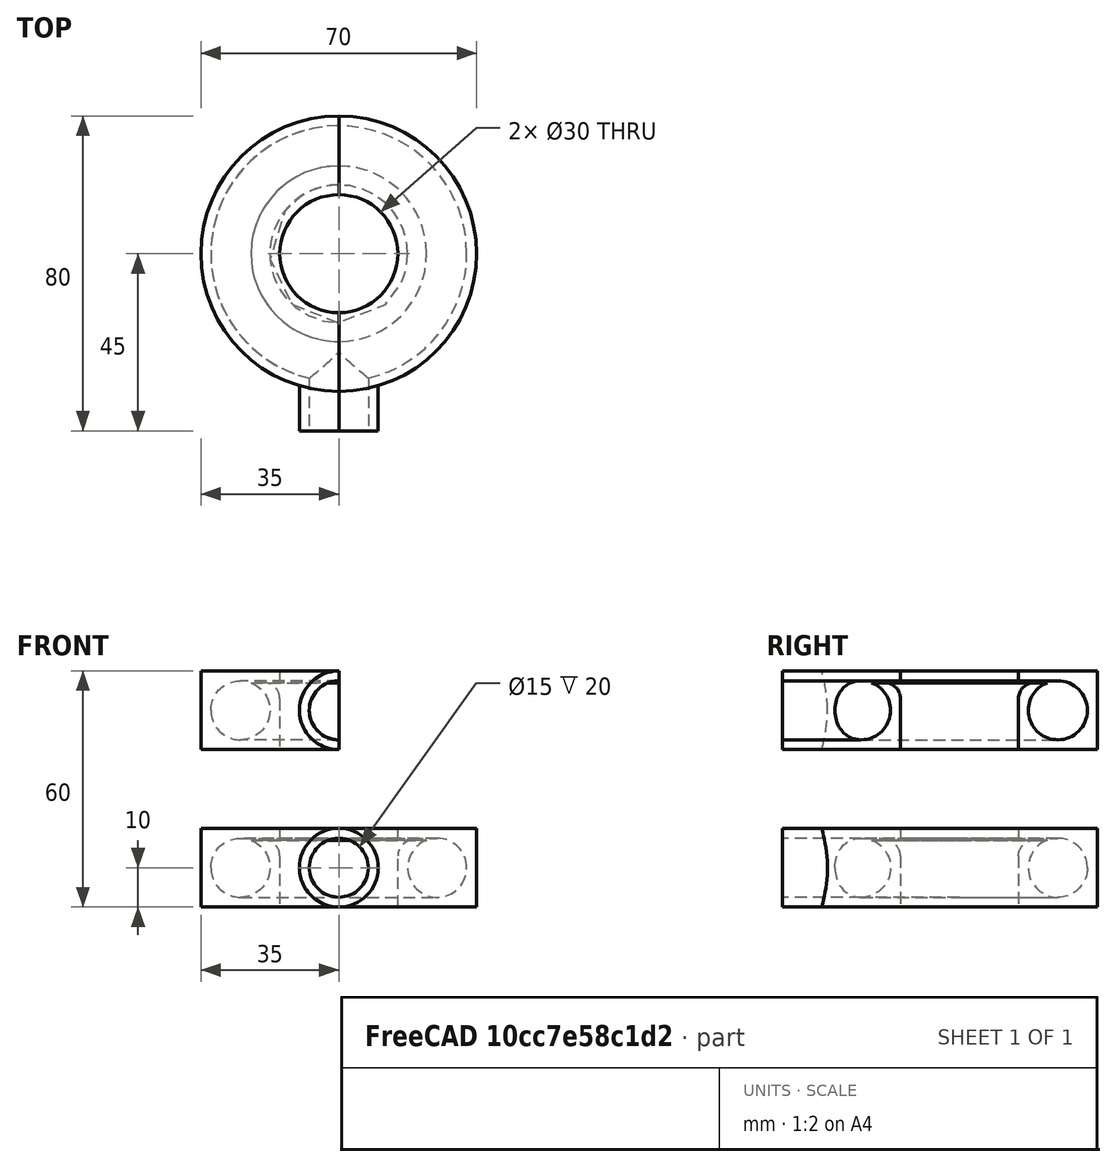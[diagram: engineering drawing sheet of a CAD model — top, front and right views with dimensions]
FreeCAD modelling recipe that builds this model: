
FCSTD DOCUMENT  (FreeCAD 1.0R)
Label: circle knife air
License: All rights reserved
objects: TechDraw::DrawViewDimension×13, Sketcher::SketchObject×11, PartDesign::Plane×6, PartDesign::Pocket×5, PartDesign::Pad×4, TechDraw::DrawProjGroupItem×4, PartDesign::Groove×2, PartDesign::Fillet×2, PartDesign::Body×2, TechDraw::DrawProjGroup×2, TechDraw::DrawSVGTemplate×1, TechDraw::DrawPage×1
note: 87 computed .brp shape members not serialized (recipe doc carries the construction recipe); baked Part::Feature solids carry a one-line shape summary decoded from their .brp

FEATURE [Sketcher::SketchObject] Sketch
  ArcFitTolerance = 1e-06
  AttachmentSupport = -> [XY_Plane]
  FullyConstrained = true
  MakeInternals = false
  MapMode = 5
  sketch-geometry (2):
    g0: Circle CenterX=0 CenterY=0 CenterZ=0 NormalX=0 NormalY=0 NormalZ=1 AngleXU=0 Radius=15
    g1: Circle CenterX=0 CenterY=0 CenterZ=0 NormalX=0 NormalY=0 NormalZ=1 AngleXU=0 Radius=35
  constraints (4):
    c: Diameter(g0) = 30
    c: Coincident(g0,g-1)
    c: Diameter(g1) = 70
    c: Coincident(g1,g0)
FEATURE [PartDesign::Pad] Pad
  Direction = (0,0,1)
  Length = 20
  Length2 = 10
  Profile = -> Sketch
  ReferenceAxis = -> Sketch [N_Axis]
  Refine = true
  Suppressed = false
  Type = 0
FEATURE [PartDesign::Plane] DatumPlane
  AttachmentOffset = pos=(0,0,0) rot=(1,0,0;1.5708rad)
  AttachmentSupport = -> [Pad]
  Length = 60
  MapMode = 5
  Placement = pos=(0,0,20) rot=(1,0,0;1.5708rad)
  ResizeMode = 0
  Width = 60
FEATURE [Sketcher::SketchObject] Sketch001
  ArcFitTolerance = 1e-06
  AttachmentSupport = -> [DatumPlane]
  ExternalGeometry = -> [Pad]
  FullyConstrained = true
  MakeInternals = false
  MapMode = 5
  Placement = pos=(0,0,20) rot=(1,0,0;1.5708rad)
  sketch-geometry (1):
    g0: Circle CenterX=25 CenterY=-10 CenterZ=0 NormalX=0 NormalY=0 NormalZ=1 AngleXU=0 Radius=7.5
  constraints (3):
    c: Diameter(g0) = 15
    c: Distance(g0,g-3) = 10
    c: DistanceY(g-3,g0) = 10
FEATURE [PartDesign::Groove] Groove
  Angle = 360
  Angle2 = 60
  Axis = (0,2e-16,1)
  Base = (0,0,20)
  BaseFeature = -> Pad
  Profile = -> Sketch001
  ReferenceAxis = -> Sketch001 [V_Axis]
  Refine = true
  Suppressed = false
  Type = 0
FEATURE [PartDesign::Plane] DatumPlane001
  AttachmentOffset = pos=(0,0,-2.5) rot=(0,0,1;0rad)
  AttachmentSupport = -> [Groove]
  Length = 60
  MapMode = 5
  Placement = pos=(0,0,17.5) rot=(0,0,1;0rad)
  ResizeMode = 0
  Width = 60
FEATURE [Sketcher::SketchObject] Sketch002
  ArcFitTolerance = 1e-06
  AttachmentSupport = -> [DatumPlane001]
  FullyConstrained = true
  MakeInternals = false
  MapMode = 5
  Placement = pos=(0,0,17.5) rot=(0,0,1;0rad)
  sketch-geometry (1):
    g0: Circle CenterX=0 CenterY=0 CenterZ=0 NormalX=0 NormalY=0 NormalZ=1 AngleXU=0 Radius=25
  constraints (2):
    c: Diameter(g0) = 50
    c: Coincident(g0,g-1)
FEATURE [PartDesign::Pocket] Pocket
  BaseFeature = -> Groove
  Direction = (0,0,-1)
  Length = 0.5
  Length2 = 5
  Profile = -> Sketch002
  ReferenceAxis = -> Sketch002 [N_Axis]
  Refine = true
  Suppressed = false
  Type = 0
FEATURE [PartDesign::Plane] DatumPlane002
  AttachmentOffset = pos=(0,-35,0) rot=(0,0.707107,0.707107;3.14159rad)
  AttachmentSupport = -> [Pocket]
  Length = 60
  MapMode = 5
  Placement = pos=(0,-35,20) rot=(0,0.707107,0.707107;3.14159rad)
  ResizeMode = 0
  Width = 60
FEATURE [Sketcher::SketchObject] Sketch003
  ArcFitTolerance = 1e-06
  AttachmentSupport = -> [DatumPlane002]
  ExternalGeometry = -> [Pocket]
  FullyConstrained = true
  MakeInternals = false
  MapMode = 5
  Placement = pos=(0,-35,20) rot=(0,0.707107,0.707107;3.14159rad)
  sketch-geometry (1):
    g0: Circle CenterX=0 CenterY=-10 CenterZ=0 NormalX=0 NormalY=0 NormalZ=1 AngleXU=0 Radius=7.5
  constraints (3):
    c: Diameter(g0) = 15
    c: PointOnObject(g0,g-2)
    c: Distance(g0,g-3) = 10
FEATURE [PartDesign::Pocket] Pocket001
  BaseFeature = -> Pocket
  Direction = (0,-1,2e-16)
  Length = 10
  Length2 = 5
  Profile = -> Sketch003 [Edge1]
  ReferenceAxis = -> Sketch003 [N_Axis]
  Refine = true
  Reversed = true
  Suppressed = false
  Type = 0
FEATURE [Sketcher::SketchObject] Sketch004
  ArcFitTolerance = 1e-06
  AttachmentSupport = -> [DatumPlane002]
  FullyConstrained = true
  MakeInternals = false
  MapMode = 5
  Placement = pos=(0,-35,20) rot=(0,0.707107,0.707107;3.14159rad)
  sketch-geometry (2):
    g0: Circle CenterX=0 CenterY=-10 CenterZ=0 NormalX=0 NormalY=0 NormalZ=1 AngleXU=0 Radius=7.5
    g1: Circle CenterX=0 CenterY=-10 CenterZ=0 NormalX=0 NormalY=0 NormalZ=1 AngleXU=0 Radius=10
  constraints (5):
    c: Diameter(g0) = 15
    c: PointOnObject(g0,g-2)
    c: DistanceY(g0,g-1) = 10
    c: Diameter(g1) = 20
    c: Coincident(g1,g0)
FEATURE [PartDesign::Pad] Pad001
  BaseFeature = -> Pocket001
  Direction = (0,1,-2e-16)
  Length = 2
  Length2 = 10
  Profile = -> Sketch004
  ReferenceAxis = -> Sketch004 [N_Axis]
  Refine = true
  Suppressed = false
  Type = 4
FEATURE [PartDesign::Fillet] Fillet
  Base = -> Pad001 [Edge15]
  BaseFeature = -> Pad001
  Radius = 4
  Refine = true
  SupportTransform = false
  Suppressed = false
  UseAllEdges = false
FEATURE [PartDesign::Body] Body
  AllowCompound = false
  Group = -> [Sketch,Pad,DatumPlane,Sketch001,Groove,DatumPlane001,Sketch002,Pocket,DatumPlane002,Sketch003,Pocket001,Sketch004,Pad001,Fillet]
  Origin = -> Origin
  Tip = -> Fillet
FEATURE [Sketcher::SketchObject] Sketch005
  ArcFitTolerance = 1e-06
  AttachmentSupport = -> [XY_Plane001]
  FullyConstrained = true
  MakeInternals = false
  MapMode = 5
  sketch-geometry (2):
    g0: Circle CenterX=0 CenterY=0 CenterZ=0 NormalX=0 NormalY=0 NormalZ=1 AngleXU=0 Radius=15
    g1: Circle CenterX=0 CenterY=0 CenterZ=0 NormalX=0 NormalY=0 NormalZ=1 AngleXU=0 Radius=35
  constraints (4):
    c: Diameter(g0) = 30
    c: Coincident(g0,g-1)
    c: Diameter(g1) = 70
    c: Coincident(g1,g0)
FEATURE [PartDesign::Pad] Pad002
  Direction = (0,0,1)
  Length = 20
  Length2 = 10
  Profile = -> Sketch005
  ReferenceAxis = -> Sketch005 [N_Axis]
  Refine = true
  Suppressed = false
  Type = 0
FEATURE [PartDesign::Plane] DatumPlane003
  AttachmentOffset = pos=(0,0,0) rot=(1,0,0;1.5708rad)
  AttachmentSupport = -> [Pad002]
  Length = 60
  MapMode = 5
  Placement = pos=(0,0,20) rot=(1,0,0;1.5708rad)
  ResizeMode = 0
  Width = 60
FEATURE [Sketcher::SketchObject] Sketch006
  ArcFitTolerance = 1e-06
  AttachmentSupport = -> [DatumPlane003]
  ExternalGeometry = -> [Pad002]
  FullyConstrained = true
  MakeInternals = false
  MapMode = 5
  Placement = pos=(0,0,20) rot=(1,0,0;1.5708rad)
  sketch-geometry (1):
    g0: Circle CenterX=25 CenterY=-10 CenterZ=0 NormalX=0 NormalY=0 NormalZ=1 AngleXU=0 Radius=7.5
  constraints (3):
    c: Diameter(g0) = 15
    c: Distance(g0,g-3) = 10
    c: DistanceY(g-3,g0) = 10
FEATURE [PartDesign::Groove] Groove001
  Angle = 360
  Angle2 = 60
  Axis = (0,2e-16,1)
  Base = (0,0,20)
  BaseFeature = -> Pad002
  Profile = -> Sketch006
  ReferenceAxis = -> Sketch006 [V_Axis]
  Refine = true
  Suppressed = false
  Type = 0
FEATURE [PartDesign::Plane] DatumPlane004
  AttachmentOffset = pos=(0,0,-2.5) rot=(0,0,1;0rad)
  AttachmentSupport = -> [Groove001]
  Length = 60
  MapMode = 5
  Placement = pos=(0,0,17.5) rot=(0,0,1;0rad)
  ResizeMode = 0
  Width = 60
FEATURE [Sketcher::SketchObject] Sketch007
  ArcFitTolerance = 1e-06
  AttachmentSupport = -> [DatumPlane004]
  FullyConstrained = true
  MakeInternals = false
  MapMode = 5
  Placement = pos=(0,0,17.5) rot=(0,0,1;0rad)
  sketch-geometry (1):
    g0: Circle CenterX=0 CenterY=0 CenterZ=0 NormalX=0 NormalY=0 NormalZ=1 AngleXU=0 Radius=25
  constraints (2):
    c: Diameter(g0) = 50
    c: Coincident(g0,g-1)
FEATURE [PartDesign::Pocket] Pocket002
  BaseFeature = -> Groove001
  Direction = (0,0,-1)
  Length = 0.5
  Length2 = 5
  Profile = -> Sketch007
  ReferenceAxis = -> Sketch007 [N_Axis]
  Refine = true
  Suppressed = false
  Type = 0
FEATURE [PartDesign::Plane] DatumPlane005
  AttachmentOffset = pos=(0,-35,0) rot=(0,0.707107,0.707107;3.14159rad)
  AttachmentSupport = -> [Pocket002]
  Length = 60
  MapMode = 5
  Placement = pos=(0,-35,20) rot=(0,0.707107,0.707107;3.14159rad)
  ResizeMode = 0
  Width = 60
FEATURE [Sketcher::SketchObject] Sketch008
  ArcFitTolerance = 1e-06
  AttachmentSupport = -> [DatumPlane005]
  ExternalGeometry = -> [Pocket002]
  FullyConstrained = true
  MakeInternals = false
  MapMode = 5
  Placement = pos=(0,-35,20) rot=(0,0.707107,0.707107;3.14159rad)
  sketch-geometry (1):
    g0: Circle CenterX=0 CenterY=-10 CenterZ=0 NormalX=0 NormalY=0 NormalZ=1 AngleXU=0 Radius=7.5
  constraints (3):
    c: Diameter(g0) = 15
    c: PointOnObject(g0,g-2)
    c: Distance(g0,g-3) = 10
FEATURE [PartDesign::Pocket] Pocket003
  BaseFeature = -> Pocket002
  Direction = (0,-1,2e-16)
  Length = 10
  Length2 = 5
  Profile = -> Sketch008 [Edge1]
  ReferenceAxis = -> Sketch008 [N_Axis]
  Refine = true
  Reversed = true
  Suppressed = false
  Type = 0
FEATURE [Sketcher::SketchObject] Sketch009
  ArcFitTolerance = 1e-06
  AttachmentSupport = -> [DatumPlane005]
  FullyConstrained = true
  MakeInternals = false
  MapMode = 5
  Placement = pos=(0,-35,20) rot=(0,0.707107,0.707107;3.14159rad)
  sketch-geometry (2):
    g0: Circle CenterX=0 CenterY=-10 CenterZ=0 NormalX=0 NormalY=0 NormalZ=1 AngleXU=0 Radius=7.5
    g1: Circle CenterX=0 CenterY=-10 CenterZ=0 NormalX=0 NormalY=0 NormalZ=1 AngleXU=0 Radius=10
  constraints (5):
    c: Diameter(g0) = 15
    c: PointOnObject(g0,g-2)
    c: DistanceY(g0,g-1) = 10
    c: Diameter(g1) = 20
    c: Coincident(g1,g0)
FEATURE [PartDesign::Pad] Pad003
  BaseFeature = -> Pocket003
  Direction = (0,1,-2e-16)
  Length = 2
  Length2 = 10
  Profile = -> Sketch009
  ReferenceAxis = -> Sketch009 [N_Axis]
  Refine = true
  Suppressed = false
  Type = 4
FEATURE [PartDesign::Fillet] Fillet001
  Base = -> Pad003 [Edge15]
  BaseFeature = -> Pad003
  Radius = 4
  Refine = true
  SupportTransform = false
  Suppressed = false
  UseAllEdges = false
FEATURE [Sketcher::SketchObject] Sketch010
  ArcFitTolerance = 1e-06
  AttachmentSupport = -> [Fillet001]
  FullyConstrained = false
  MakeInternals = false
  MapMode = 5
  Placement = pos=(0,0,20) rot=(0,0,1;0rad)
  sketch-geometry (4):
    g0: LineSegment StartX=0 StartY=40.2056 StartZ=0 EndX=0 EndY=-51.8997 EndZ=0
    g1: LineSegment StartX=0 StartY=-51.8997 StartZ=0 EndX=42.0981 EndY=-51.8997 EndZ=0
    g2: LineSegment StartX=42.0981 StartY=-51.8997 StartZ=0 EndX=42.0981 EndY=40.2056 EndZ=0
    g3: LineSegment StartX=42.0981 StartY=40.2056 StartZ=0 EndX=0 EndY=40.2056 EndZ=0
  constraints (9):
    c: Coincident(g0,g1)
    c: Coincident(g1,g2)
    c: Coincident(g2,g3)
    c: Coincident(g3,g0)
    c: Vertical(g0)
    c: Vertical(g2)
    c: Horizontal(g1)
    c: Horizontal(g3)
    c: PointOnObject(g0,g-2)
FEATURE [PartDesign::Pocket] Pocket004
  BaseFeature = -> Fillet001
  Direction = (0,0,-1)
  Length = 5
  Length2 = 5
  Profile = -> Sketch010
  ReferenceAxis = -> Sketch010 [N_Axis]
  Refine = true
  Suppressed = false
  Type = 1
FEATURE [PartDesign::Body] Body001
  AllowCompound = false
  Group = -> [Sketch005,Pad002,DatumPlane003,Sketch006,Groove001,DatumPlane004,Sketch007,Pocket002,DatumPlane005,Sketch008,Pocket003,Sketch009,Pad003,Fillet001,Sketch010,Pocket004]
  Origin = -> Origin001
  Placement = pos=(0,0,40) rot=(0,0,1;0rad)
  Tip = -> Pocket004
FEATURE [TechDraw::DrawSVGTemplate] Template
  EditableTexts = approval_person=B. Hecate; creator=A. Nemesis; date_of_issue=27/10/25; document_type=Assembly Drawing; general_tolerances=ISO 2768-m; identification_number=DN; language_code=EN; part_material=Stainless steel Mat.No. 1.4301; revision_index=AAA; sheet_number=1 / 1; sheet_scale=1 : 1; title=circle knife air
  Height = 210
  Orientation = 1
  Template = <path>
  Width = 297
FEATURE [TechDraw::DrawProjGroupItem] View  label="Front001"
  CoarseView = false
  Direction = (1,-1e-16,0)
  Focus = 100
  HardHidden = false
  IsoCount = 0
  IsoHidden = false
  IsoVisible = false
  LockPosition = true
  Perspective = false
  Rotation = 0
  RotationVector = (1,0,0)
  ScaleType = 2
  ScrubCount = 1
  SeamHidden = false
  SeamVisible = false
  SmoothHidden = false
  SmoothVisible = true
  Source = -> [Body001]
  Type = 0
  X = 0
  XDirection = (1e-16,1,0)
  Y = 0
FEATURE [TechDraw::DrawProjGroupItem] View001  label="Front"
  CoarseView = false
  Direction = (0,-1,0)
  Focus = 100
  HardHidden = false
  IsoCount = 0
  IsoHidden = false
  IsoVisible = false
  LockPosition = true
  Perspective = false
  Rotation = 0
  RotationVector = (1,0,0)
  ScaleType = 2
  ScrubCount = 1
  SeamHidden = false
  SeamVisible = false
  SmoothHidden = false
  SmoothVisible = true
  Source = -> [Body]
  Type = 0
  X = 0
  XDirection = (1,0,0)
  Y = 0
FEATURE [TechDraw::DrawProjGroupItem] ProjItem  label="Top"
  CoarseView = false
  Direction = (0,0,1)
  Focus = 100
  HardHidden = false
  IsoCount = 0
  IsoHidden = false
  IsoVisible = false
  LockPosition = false
  Perspective = false
  Rotation = 0
  RotationVector = (1,0,0)
  ScaleType = 0
  ScrubCount = 1
  SeamHidden = false
  SeamVisible = false
  SmoothHidden = false
  SmoothVisible = true
  Source = -> [Body]
  Type = 4
  X = 0
  XDirection = (1,0,0)
  Y = -65
FEATURE [TechDraw::DrawProjGroup] ProjGroup
  Anchor = -> View001
  AutoDistribute = true
  LockPosition = false
  ProjectionType = 0
  Rotation = 0
  ScaleType = 0
  Source = -> [Body]
  Views = -> [View001,ProjItem]
  X = 194.823
  Y = 180.18
  spacingX = 15
  spacingY = 15
FEATURE [TechDraw::DrawViewDimension] Dimension
  AngleOverride = false
  Arbitrary = false
  ArbitraryTolerances = false
  BoxCorners = (2) [(-35,-40,-1e-07),(35,40,1e-07)]
  EqualTolerance = true
  ExtensionAngle = 0
  FormatSpec = ⌀%.2w
  FormatSpecOverTolerance = %+.2w
  FormatSpecUnderTolerance = %+.2w
  Inverted = false
  LineAngle = 0
  LockPosition = false
  MeasureType = 1
  OverTolerance = 0
  References2D = -> [ProjItem]
  Rotation = 0
  ScaleType = 0
  TheoreticalExact = false
  Type = 5
  UnderTolerance = 0
  X = 47.9854
  Y = 2.55014
FEATURE [TechDraw::DrawViewDimension] Dimension001
  AngleOverride = false
  Arbitrary = false
  ArbitraryTolerances = false
  BoxCorners = (2) [(-35,-40,-1e-07),(35,40,1e-07)]
  EqualTolerance = true
  ExtensionAngle = 0
  FormatSpec = R%.2w
  FormatSpecOverTolerance = %+.2w
  FormatSpecUnderTolerance = %+.2w
  Inverted = false
  LineAngle = 0
  LockPosition = false
  MeasureType = 1
  OverTolerance = 0
  References2D = -> [ProjItem]
  Rotation = 0
  ScaleType = 0
  TheoreticalExact = false
  Type = 4
  UnderTolerance = 0
  X = 50.0135
  Y = 13.0677
FEATURE [TechDraw::DrawViewDimension] Dimension002
  AngleOverride = false
  Arbitrary = false
  ArbitraryTolerances = false
  BoxCorners = (2) [(-35,-40,-1e-07),(35,40,1e-07)]
  EqualTolerance = true
  ExtensionAngle = 0
  FormatSpec = %.2w
  FormatSpecOverTolerance = %+.2w
  FormatSpecUnderTolerance = %+.2w
  Inverted = false
  LineAngle = 0
  LockPosition = false
  MeasureType = 1
  OverTolerance = 0
  References2D = -> [ProjItem]
  Rotation = 0
  ScaleType = 0
  TheoreticalExact = false
  Type = 2
  UnderTolerance = 0
  X = 22.9103
  Y = -34.2705
FEATURE [TechDraw::DrawViewDimension] Dimension003
  AngleOverride = false
  Arbitrary = false
  ArbitraryTolerances = false
  BoxCorners = (2) [(-35,-40,-1e-07),(35,40,1e-07)]
  EqualTolerance = true
  ExtensionAngle = 0
  FormatSpec = %.2w
  FormatSpecOverTolerance = %+.2w
  FormatSpecUnderTolerance = %+.2w
  Inverted = false
  LineAngle = 0
  LockPosition = false
  MeasureType = 1
  OverTolerance = 0
  References2D = -> [ProjItem]
  Rotation = 0
  ScaleType = 0
  TheoreticalExact = false
  Type = 0
  UnderTolerance = 0
  X = -22.6694
  Y = -43.2394
FEATURE [TechDraw::DrawViewDimension] Dimension004
  AngleOverride = false
  Arbitrary = false
  ArbitraryTolerances = false
  BoxCorners = (2) [(-35,-10,-1e-07),(35,10,1e-07)]
  EqualTolerance = true
  ExtensionAngle = 0
  FormatSpec = ⌀%.2w
  FormatSpecOverTolerance = %+.2w
  FormatSpecUnderTolerance = %+.2w
  Inverted = false
  LineAngle = 0
  LockPosition = false
  MeasureType = 1
  OverTolerance = 0
  References2D = -> [View001]
  Rotation = 0
  ScaleType = 0
  TheoreticalExact = false
  Type = 5
  UnderTolerance = 0
  X = 23.2593
  Y = 3.16016
FEATURE [TechDraw::DrawViewDimension] Dimension005
  AngleOverride = false
  Arbitrary = false
  ArbitraryTolerances = false
  BoxCorners = (2) [(-35,-10,-1e-07),(35,10,1e-07)]
  EqualTolerance = true
  ExtensionAngle = 0
  FormatSpec = ⌀%.2w
  FormatSpecOverTolerance = %+.2w
  FormatSpecUnderTolerance = %+.2w
  Inverted = false
  LineAngle = 0
  LockPosition = false
  MeasureType = 1
  OverTolerance = 0
  References2D = -> [View001]
  Rotation = 0
  ScaleType = 0
  TheoreticalExact = false
  Type = 5
  UnderTolerance = 0
  X = -22.5208
  Y = -0.76623
FEATURE [TechDraw::DrawViewDimension] Dimension006
  AngleOverride = false
  Arbitrary = false
  ArbitraryTolerances = false
  BoxCorners = (2) [(-35,-10,-1e-07),(35,10,1e-07)]
  EqualTolerance = true
  ExtensionAngle = 0
  FormatSpec = %.2w
  FormatSpecOverTolerance = %+.2w
  FormatSpecUnderTolerance = %+.2w
  Inverted = false
  LineAngle = 0
  LockPosition = false
  MeasureType = 1
  OverTolerance = 0
  References2D = -> [View001]
  Rotation = 0
  ScaleType = 0
  TheoreticalExact = false
  Type = 2
  UnderTolerance = 0
  X = 42.451
  Y = 0
FEATURE [TechDraw::DrawViewDimension] Dimension007
  AngleOverride = false
  Arbitrary = false
  ArbitraryTolerances = false
  BoxCorners = (2) [(-60,-15,-1e-07),(60,15,1e-07)]
  EqualTolerance = true
  ExtensionAngle = 0
  FormatSpec = R%.2w
  FormatSpecOverTolerance = %+.2w
  FormatSpecUnderTolerance = %+.2w
  Inverted = false
  LineAngle = 0
  LockPosition = false
  MeasureType = 1
  OverTolerance = 0
  References2D = -> [View]
  Rotation = 0
  ScaleType = 0
  TheoreticalExact = false
  Type = 4
  UnderTolerance = 0
  X = 73.229
  Y = 4.36548
FEATURE [TechDraw::DrawViewDimension] Dimension008
  AngleOverride = false
  Arbitrary = false
  ArbitraryTolerances = false
  BoxCorners = (2) [(-60,-15,-1e-07),(60,15,1e-07)]
  EqualTolerance = true
  ExtensionAngle = 0
  FormatSpec = R%.2w
  FormatSpecOverTolerance = %+.2w
  FormatSpecUnderTolerance = %+.2w
  Inverted = false
  LineAngle = 0
  LockPosition = false
  MeasureType = 1
  OverTolerance = 0
  References2D = -> [View]
  Rotation = 0
  ScaleType = 0
  TheoreticalExact = false
  Type = 4
  UnderTolerance = 0
  X = 15.9414
  Y = 26.6435
FEATURE [TechDraw::DrawViewDimension] Dimension009
  AngleOverride = false
  Arbitrary = false
  ArbitraryTolerances = false
  BoxCorners = (2) [(-60,-15,-1e-07),(60,15,1e-07)]
  EqualTolerance = true
  ExtensionAngle = 0
  FormatSpec = %.2w
  FormatSpecOverTolerance = %+.2w
  FormatSpecUnderTolerance = %+.2w
  Inverted = false
  LineAngle = 0
  LockPosition = false
  MeasureType = 1
  OverTolerance = 0
  References2D = -> [View]
  Rotation = 0
  ScaleType = 0
  TheoreticalExact = false
  Type = 0
  UnderTolerance = 0
  X = -72.5144
  Y = 25.9519
FEATURE [TechDraw::DrawProjGroupItem] ProjItem002  label="FrontTopRight"
  CoarseView = false
  Direction = (0.57735,0.57735,0.57735)
  Focus = 100
  HardHidden = false
  IsoCount = 0
  IsoHidden = false
  IsoVisible = false
  LockPosition = false
  Perspective = false
  Rotation = 0
  RotationVector = (1,0,0)
  ScaleType = 0
  ScrubCount = 1
  SeamHidden = false
  SeamVisible = false
  SmoothHidden = false
  SmoothVisible = true
  Source = -> [Body001]
  Type = 7
  X = -0.480059
  XDirection = (-0.707107,0.707107,0)
  Y = -52.6174
FEATURE [TechDraw::DrawProjGroup] ProjGroup001
  Anchor = -> View
  AutoDistribute = true
  LockPosition = false
  ProjectionType = 0
  Rotation = 0
  ScaleType = 2
  Source = -> [Body001]
  Views = -> [View,ProjItem002]
  X = 80.108
  Y = 166.855
  spacingX = 15
  spacingY = 15
FEATURE [TechDraw::DrawViewDimension] Dimension010
  AngleOverride = false
  Arbitrary = false
  ArbitraryTolerances = false
  BoxCorners = (2) [(-40,-10,-1e-07),(40,10,1e-07)]
  EqualTolerance = true
  ExtensionAngle = 0
  FormatSpec = R%.2w
  FormatSpecOverTolerance = %+.2w
  FormatSpecUnderTolerance = %+.2w
  Inverted = false
  LineAngle = 0
  LockPosition = false
  MeasureType = 1
  OverTolerance = 0
  References2D = -> [View]
  Rotation = 0
  ScaleType = 0
  TheoreticalExact = false
  Type = 4
  UnderTolerance = 0
  X = 11.6188
  Y = 21.0217
FEATURE [TechDraw::DrawViewDimension] Dimension011
  AngleOverride = false
  Arbitrary = false
  ArbitraryTolerances = false
  BoxCorners = (2) [(-40,-10,-1e-07),(40,10,1e-07)]
  EqualTolerance = true
  ExtensionAngle = 0
  FormatSpec = R%.2w
  FormatSpecOverTolerance = %+.2w
  FormatSpecUnderTolerance = %+.2w
  Inverted = false
  LineAngle = 0
  LockPosition = false
  MeasureType = 1
  OverTolerance = 0
  References2D = -> [View]
  Rotation = 0
  ScaleType = 0
  TheoreticalExact = false
  Type = 4
  UnderTolerance = 0
  X = 51.4806
  Y = 15.5919
FEATURE [TechDraw::DrawViewDimension] Dimension012
  AngleOverride = false
  Arbitrary = false
  ArbitraryTolerances = false
  BoxCorners = (2) [(-40,-10,-1e-07),(40,10,1e-07)]
  EqualTolerance = true
  ExtensionAngle = 0
  FormatSpec = %.2w
  FormatSpecOverTolerance = %+.2w
  FormatSpecUnderTolerance = %+.2w
  Inverted = false
  LineAngle = 0
  LockPosition = false
  MeasureType = 1
  OverTolerance = 0
  References2D = -> [View]
  Rotation = 0
  ScaleType = 0
  TheoreticalExact = false
  Type = 0
  UnderTolerance = 0
  X = -55.763
  Y = 18.8591
FEATURE [TechDraw::DrawPage] Page
  KeepUpdated = true
  NextBalloonIndex = 1
  ProjectionType = 0
  Template = -> Template
  Views = -> [ProjGroup,Dimension,Dimension001,Dimension002,Dimension003,Dimension004,Dimension005,Dimension006,Dimension007,Dimension008,Dimension009,ProjGroup001,Dimension010,Dimension011,Dimension012]
note: 1 file-system path scrubbed to <path> (originals preserved in the JSON sidecar)
